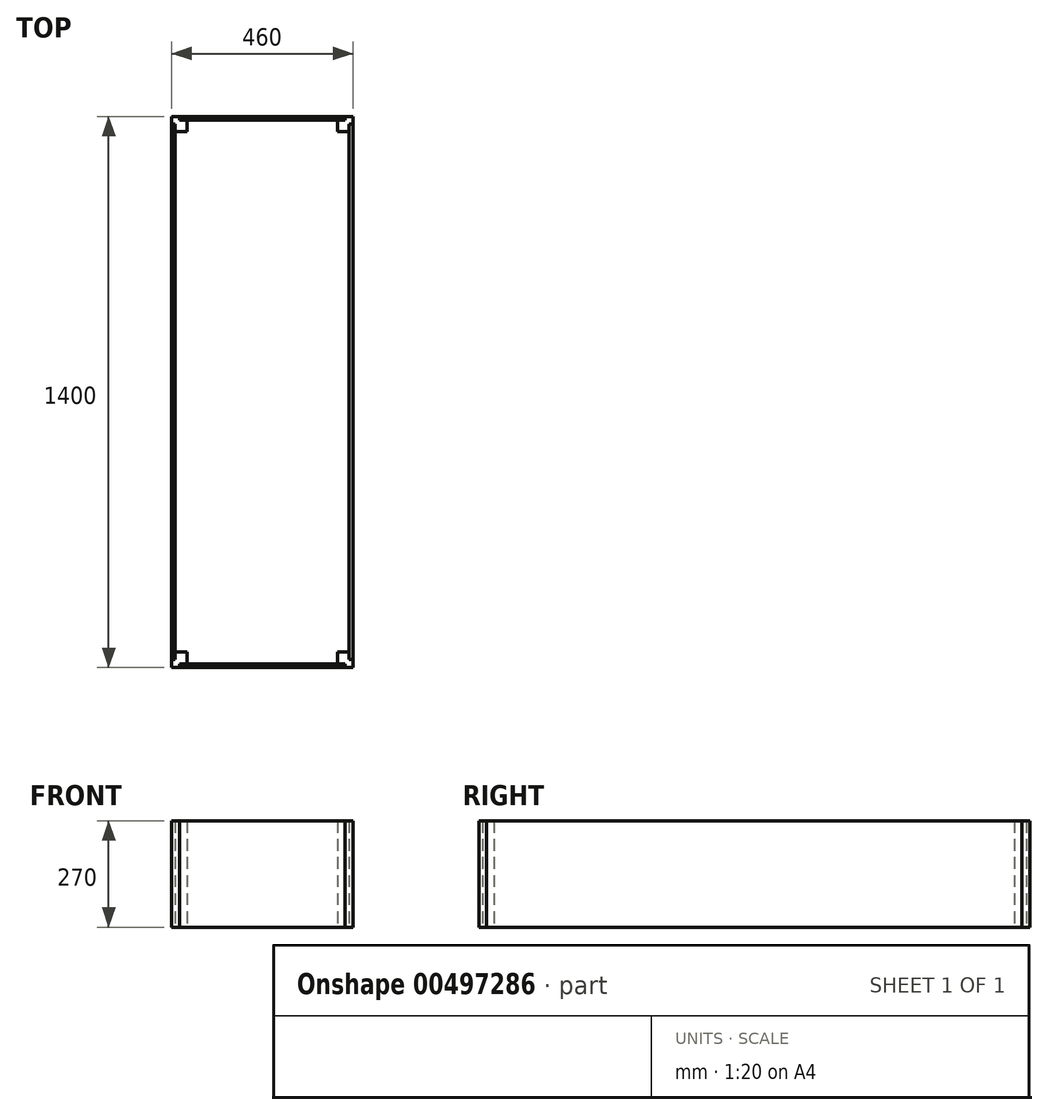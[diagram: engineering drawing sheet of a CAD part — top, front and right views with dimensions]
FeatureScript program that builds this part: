
annotation { "Feature Type Name" : "Feature", "Feature Type Description" : "" }
export const myFeature = defineFeature(function(context is Context, id is Id, definition is map)
    precondition{}
    {
        {
            var Q0;
            Q0=qCreatedBy(makeId("Top.planeOp"),FACE);
            var sketch = newSketch(context, id + "F0", { "sketchPlane" : qUnion([Q0])});
            skLineSegment(sketch, "E0.bottom", {"start": v(-230, 700) * mm, "end": v(230, 700) * mm, "construction": true});
            skLineSegment(sketch, "E0.top", {"start": v(-230, -700) * mm, "end": v(230, -700) * mm, "construction": true});
            skLineSegment(sketch, "E0.left", {"start": v(-230, 700) * mm, "end": v(-230, -700) * mm, "construction": true});
            skLineSegment(sketch, "E0.right", {"start": v(230, 700) * mm, "end": v(230, -700) * mm, "construction": true});
            skLineSegment(sketch, "E1.bottom", {"start": v(-230, 700) * mm, "end": v(-210, 700) * mm});
            skLineSegment(sketch, "E1.top", {"start": v(-221, 661) * mm, "end": v(-191, 661) * mm});
            skLineSegment(sketch, "E1.left", {"start": v(-230, 700) * mm, "end": v(-230, 680) * mm});
            skLineSegment(sketch, "E1.right", {"start": v(-191, 691) * mm, "end": v(-191, 661) * mm});
            skLineSegment(sketch, "E2", {"start": v(0, 700) * mm, "end": v(0, -700) * mm, "construction": true});
            skLineSegment(sketch, "E3", {"start": v(230, 0) * mm, "end": v(-225.07, 0) * mm, "construction": true});
            skLineSegment(sketch, "E4", {"start": v(-210, 700) * mm, "end": v(-210, 691) * mm});
            skLineSegment(sketch, "E5", {"start": v(-210, 691) * mm, "end": v(-191, 691) * mm});
            skLineSegment(sketch, "E6", {"start": v(-230, 680) * mm, "end": v(-221, 680) * mm});
            skLineSegment(sketch, "E7", {"start": v(-221, 680) * mm, "end": v(-221, 661) * mm});
            skLineSegment(sketch, "E8.MirrorCS", {"start": v(191, 691) * mm, "end": v(191, 661) * mm});
            skLineSegment(sketch, "E9.MirrorCS", {"start": v(210, 691) * mm, "end": v(191, 691) * mm});
            skLineSegment(sketch, "E10.MirrorCS", {"start": v(210, 700) * mm, "end": v(210, 691) * mm});
            skLineSegment(sketch, "E11.MirrorCS", {"start": v(230, 700) * mm, "end": v(210, 700) * mm});
            skLineSegment(sketch, "E12.MirrorCS", {"start": v(230, 700) * mm, "end": v(230, 680) * mm});
            skLineSegment(sketch, "E13.MirrorCS", {"start": v(230, 680) * mm, "end": v(221, 680) * mm});
            skLineSegment(sketch, "E14.MirrorCS", {"start": v(221, 680) * mm, "end": v(221, 661) * mm});
            skLineSegment(sketch, "E15.MirrorCS", {"start": v(221, 661) * mm, "end": v(191, 661) * mm});
            skLineSegment(sketch, "E16.MirrorCS", {"start": v(-191, -691) * mm, "end": v(-191, -661) * mm});
            skLineSegment(sketch, "E17.MirrorCS", {"start": v(-210, -691) * mm, "end": v(-191, -691) * mm});
            skLineSegment(sketch, "E18.MirrorCS", {"start": v(-210, -700) * mm, "end": v(-210, -691) * mm});
            skLineSegment(sketch, "E19.MirrorCS", {"start": v(-230, -700) * mm, "end": v(-210, -700) * mm});
            skLineSegment(sketch, "E20.MirrorCS", {"start": v(-230, -700) * mm, "end": v(-230, -680) * mm});
            skLineSegment(sketch, "E21.MirrorCS", {"start": v(-230, -680) * mm, "end": v(-221, -680) * mm});
            skLineSegment(sketch, "E22.MirrorCS", {"start": v(-221, -680) * mm, "end": v(-221, -661) * mm});
            skLineSegment(sketch, "E23.MirrorCS", {"start": v(-221, -661) * mm, "end": v(-191, -661) * mm});
            skLineSegment(sketch, "E24.MirrorCS", {"start": v(221, -661) * mm, "end": v(191, -661) * mm});
            skLineSegment(sketch, "E25.MirrorCS", {"start": v(191, -691) * mm, "end": v(191, -661) * mm});
            skLineSegment(sketch, "E26.MirrorCS", {"start": v(210, -691) * mm, "end": v(191, -691) * mm});
            skLineSegment(sketch, "E27.MirrorCS", {"start": v(221, -680) * mm, "end": v(221, -661) * mm});
            skLineSegment(sketch, "E28.MirrorCS", {"start": v(230, -700) * mm, "end": v(210, -700) * mm});
            skLineSegment(sketch, "E29.MirrorCS", {"start": v(230, -700) * mm, "end": v(230, -680) * mm});
            skLineSegment(sketch, "E30.MirrorCS", {"start": v(230, -680) * mm, "end": v(221, -680) * mm});
            skLineSegment(sketch, "E31.MirrorCS", {"start": v(210, -700) * mm, "end": v(210, -691) * mm});
            skLineSegment(sketch, "E32.left", {"start": v(-230, 680) * mm, "end": v(-230, -680) * mm});
            skLineSegment(sketch, "E32.right", {"start": v(-221, 680) * mm, "end": v(-221, -680) * mm});
            skLineSegment(sketch, "E33.bottom", {"start": v(-210, -691) * mm, "end": v(210, -691) * mm});
            skLineSegment(sketch, "E33.top", {"start": v(-210, -700) * mm, "end": v(210, -700) * mm});
            skLineSegment(sketch, "E33.left", {"start": v(-210, -691) * mm, "end": v(-210, -700) * mm});
            skLineSegment(sketch, "E33.right", {"start": v(210, -691) * mm, "end": v(210, -700) * mm});
            skLineSegment(sketch, "E34.bottom", {"start": v(221, -680) * mm, "end": v(230, -680) * mm});
            skLineSegment(sketch, "E34.top", {"start": v(221, 680) * mm, "end": v(230, 680) * mm});
            skLineSegment(sketch, "E34.left", {"start": v(221, -680) * mm, "end": v(221, 680) * mm});
            skLineSegment(sketch, "E34.right", {"start": v(230, -680) * mm, "end": v(230, 680) * mm});
            skLineSegment(sketch, "E35.bottom", {"start": v(-210, 700) * mm, "end": v(210, 700) * mm});
            skLineSegment(sketch, "E35.top", {"start": v(-210, 691) * mm, "end": v(210, 691) * mm});
            skSolve(sketch);
        }
        {
            assignVariable(context, id + "F1", {"name" : "height", "anyValue" : 270});
        }
        {
            var Q0;
            Q0=makeQuery(id+"F0.imprint","IMPRINT",FACE,{"disambiguationData":[TD([[makeQuery(id+"F0.imprint","IMPRINT",EDGE,{"derivedFrom":sQuery(id+"F0.wireOp",EDGE,"E1.bottom")}),-1.0]])]});
            extrude(context, id + "F2", {"entities" : qUnion([Q0]), "depth" : (getVariable(context, 'height')) * mm});
        }
        {
            var Q0;
            Q0=makeQuery(id+"F2.opExtrude","SWEPT_BODY",BODY,{"disambiguationData":[OSD([sQuery(id+"F0.wireOp",EDGE,"E1.bottom"),sQuery(id+"F0.wireOp",EDGE,"E1.top"),sQuery(id+"F0.wireOp",EDGE,"E1.left"),sQuery(id+"F0.wireOp",EDGE,"E1.right"),sQuery(id+"F0.wireOp",EDGE,"E6"),sQuery(id+"F0.wireOp",EDGE,"E32.right"),sQuery(id+"F0.wireOp",EDGE,"E35.top"),sQuery(id+"F0.wireOp",EDGE,"E4")])]});
            var Q1;
            Q1=qCreatedBy(makeId("Right.planeOp"),FACE);
            mirror(context, id + "F3", {"entities" : qUnion([Q0]), "mirrorPlane" : qUnion([Q1])});
        }
        {
            var Q0;
            Q0=makeQuery(id+"F2.opExtrude","SWEPT_BODY",BODY,{"disambiguationData":[OSD([sQuery(id+"F0.wireOp",EDGE,"E1.bottom"),sQuery(id+"F0.wireOp",EDGE,"E1.top"),sQuery(id+"F0.wireOp",EDGE,"E1.left"),sQuery(id+"F0.wireOp",EDGE,"E1.right"),sQuery(id+"F0.wireOp",EDGE,"E6"),sQuery(id+"F0.wireOp",EDGE,"E32.right"),sQuery(id+"F0.wireOp",EDGE,"E35.top"),sQuery(id+"F0.wireOp",EDGE,"E4")])]});
            var Q1;
            Q1=makeQuery(id+"F3.opPattern","COPY",BODY,{"derivedFrom":makeQuery(id+"F2.opExtrude","SWEPT_BODY",BODY,{"disambiguationData":[OSD([sQuery(id+"F0.wireOp",EDGE,"E1.bottom"),sQuery(id+"F0.wireOp",EDGE,"E1.top"),sQuery(id+"F0.wireOp",EDGE,"E1.left"),sQuery(id+"F0.wireOp",EDGE,"E1.right"),sQuery(id+"F0.wireOp",EDGE,"E6"),sQuery(id+"F0.wireOp",EDGE,"E32.right"),sQuery(id+"F0.wireOp",EDGE,"E35.top"),sQuery(id+"F0.wireOp",EDGE,"E4")])]}),"instanceName":"1"});
            var Q2;
            Q2=qCreatedBy(makeId("Front.planeOp"),FACE);
            mirror(context, id + "F4", {"entities" : qUnion([Q0, Q1]), "mirrorPlane" : qUnion([Q2])});
        }
        {
            var Q0;
            {var subQ2=sQuery(id+"F0.wireOp",EDGE,"E6");Q0=makeQuery(id+"F0.imprint","IMPRINT",FACE,{"disambiguationData":[TD([[makeQuery(id+"F0.imprint","IMPRINT",EDGE,{"derivedFrom":subQ2}),-1.0]])]});}
            extrude(context, id + "F5", {"entities" : qUnion([Q0]), "depth" : (getVariable(context, 'height')) * mm});
        }
        {
            var Q0;
            Q0=makeQuery(id+"F5.opExtrude","SWEPT_BODY",BODY,{"disambiguationData":[OSD([sQuery(id+"F0.wireOp",EDGE,"E6"),sQuery(id+"F0.wireOp",EDGE,"E21.MirrorCS"),sQuery(id+"F0.wireOp",EDGE,"E32.left"),sQuery(id+"F0.wireOp",EDGE,"E32.right")])]});
            var Q1;
            Q1=qCreatedBy(makeId("Right.planeOp"),FACE);
            mirror(context, id + "F6", {"entities" : qUnion([Q0]), "mirrorPlane" : qUnion([Q1])});
        }
        {
            var Q0;
            Q0=makeQuery(id+"F0.imprint","IMPRINT",FACE,{"disambiguationData":[TD([[makeQuery(id+"F0.imprint","IMPRINT",EDGE,{"derivedFrom":sQuery(id+"F0.wireOp",EDGE,"E35.bottom")}),-1.0]])]});
            extrude(context, id + "F7", {"entities" : qUnion([Q0]), "depth" : getVariable(context, 'height') * mm});
        }
        {
            var Q0;
            Q0=makeQuery(id+"F7.opExtrude","SWEPT_BODY",BODY,{"disambiguationData":[OSD([sQuery(id+"F0.wireOp",EDGE,"E35.bottom"),sQuery(id+"F0.wireOp",EDGE,"E35.top"),sQuery(id+"F0.wireOp",EDGE,"E4"),sQuery(id+"F0.wireOp",EDGE,"E10.MirrorCS")])]});
            var Q1;
            Q1=qCreatedBy(makeId("Front.planeOp"),FACE);
            mirror(context, id + "F8", {"entities" : qUnion([Q0]), "mirrorPlane" : qUnion([Q1])});
        }
    });
